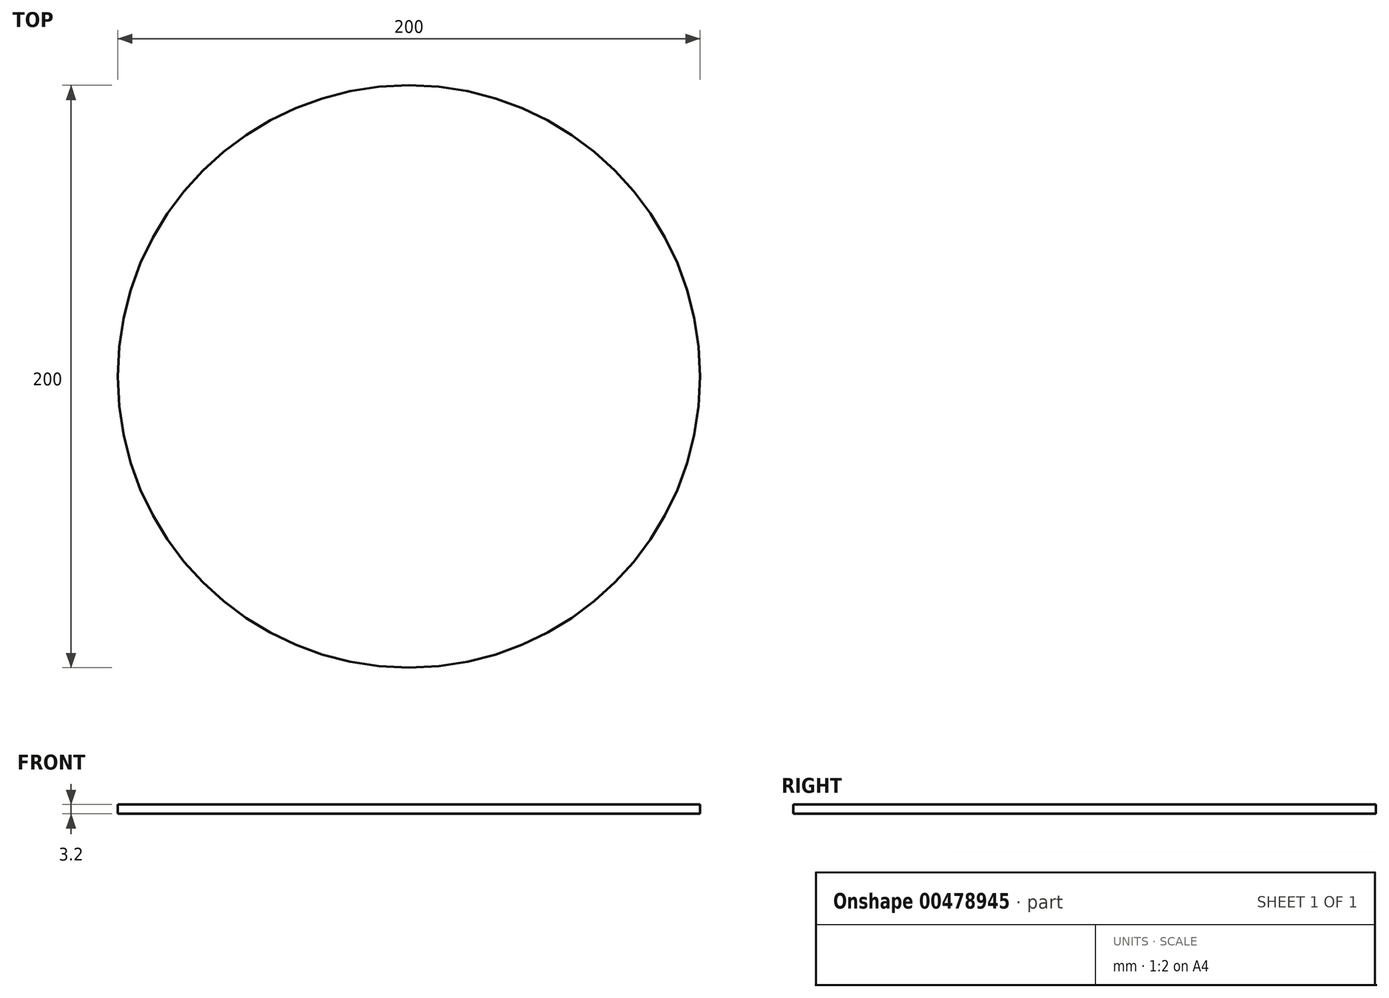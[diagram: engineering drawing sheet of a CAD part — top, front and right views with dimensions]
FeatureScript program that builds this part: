
annotation { "Feature Type Name" : "Feature", "Feature Type Description" : "" }
export const myFeature = defineFeature(function(context is Context, id is Id, definition is map)
    precondition{}
    {
        {
            var Q0;
            Q0=qCreatedBy(makeId("Top.planeOp"),FACE);
            var sketch = newSketch(context, id + "F0", { "sketchPlane" : qUnion([Q0])});
            skCircle(sketch, "E0", {"center": v(0, 0) * mm, "radius": 100 * mm});
            skSolve(sketch);
        }
        {
            var Q0;
            Q0=makeQuery(id+"F0.imprint","IMPRINT",FACE,{"disambiguationData":[TD([[makeQuery(id+"F0.imprint","IMPRINT",EDGE,{"derivedFrom":sQuery(id+"F0.wireOp",EDGE,"E0")}),1.0]])]});
            extrude(context, id + "F1", {"entities" : qUnion([Q0]), "depth" : 3.2 * mm});
        }
    });
